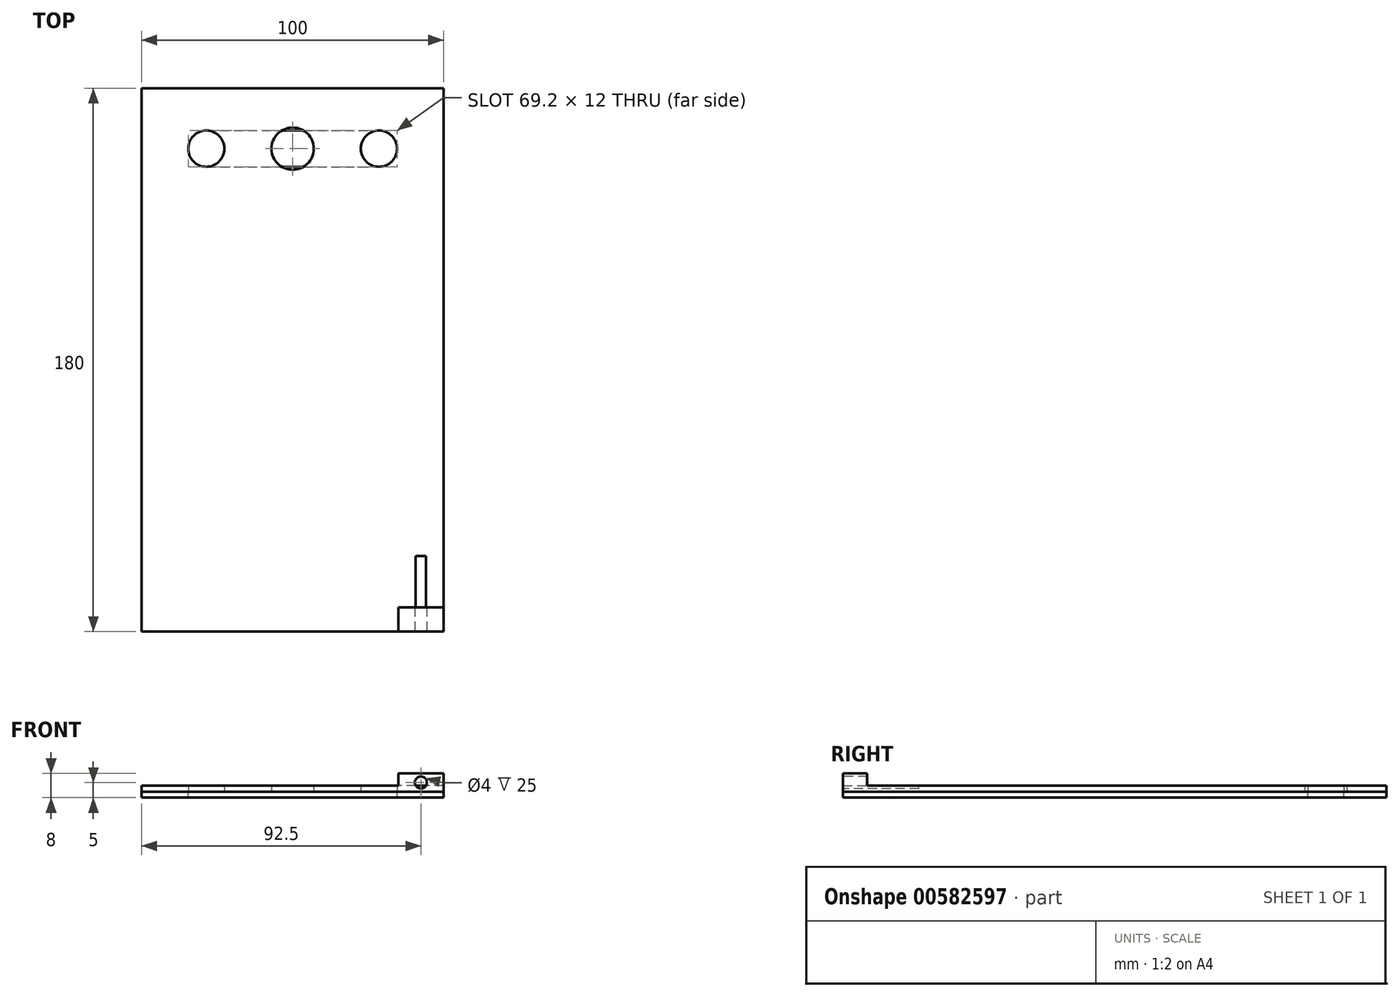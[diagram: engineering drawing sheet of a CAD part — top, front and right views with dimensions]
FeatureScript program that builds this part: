
annotation { "Feature Type Name" : "Feature", "Feature Type Description" : "" }
export const myFeature = defineFeature(function(context is Context, id is Id, definition is map)
    precondition{}
    {
        {
            var Q0;
            Q0=qCreatedBy(makeId("Top.planeOp"),FACE);
            var sketch = newSketch(context, id + "F0", { "sketchPlane" : qUnion([Q0])});
            skLineSegment(sketch, "E0.bottom", {"start": v(-50, -90) * mm, "end": v(50, -90) * mm});
            skLineSegment(sketch, "E0.top", {"start": v(-50, 90) * mm, "end": v(50, 90) * mm});
            skLineSegment(sketch, "E0.left", {"start": v(-50, -90) * mm, "end": v(-50, 90) * mm});
            skLineSegment(sketch, "E0.right", {"start": v(50, -90) * mm, "end": v(50, 90) * mm});
            skPoint(sketch, "E0.middle", {"position": v(0, 0) * mm});
            skCircle(sketch, "E1", {"center": v(0, 70) * mm, "radius": 7 * mm});
            skCircle(sketch, "E2", {"center": v(-28.6, 70) * mm, "radius": 6 * mm});
            skCircle(sketch, "E3.MirrorC", {"center": v(28.6, 70) * mm, "radius": 6 * mm});
            skSolve(sketch);
        }
        {
            var Q0;
            Q0 = qSketchRegion(id + "F0", true);
            extrude(context, id + "F1", {"entities" : qUnion([Q0]), "depth" : 2 * mm, "offsetDistance" : 25 * mm});
        }
        {
            var Q0;
            Q0=makeQuery(id+"F1.opExtrude","CAP_FACE",FACE,{"disambiguationData":[OSD([sQuery(id+"F0.wireOp",EDGE,"E0.bottom"),sQuery(id+"F0.wireOp",EDGE,"E0.top"),sQuery(id+"F0.wireOp",EDGE,"E0.left"),sQuery(id+"F0.wireOp",EDGE,"E0.right"),sQuery(id+"F0.wireOp",EDGE,"E1")])],"isStart":true});
            var sketch = newSketch(context, id + "F2", { "sketchPlane" : qUnion([Q0])});
            skLineSegment(sketch, "E4.bottom", {"start": v(-50, 90) * mm, "end": v(50, 90) * mm});
            skLineSegment(sketch, "E4.top", {"start": v(-50, -90) * mm, "end": v(50, -90) * mm});
            skLineSegment(sketch, "E4.left", {"start": v(-50, 90) * mm, "end": v(-50, -90) * mm});
            skLineSegment(sketch, "E4.right", {"start": v(50, 90) * mm, "end": v(50, -90) * mm});
            skCircle(sketch, "E5.0", {"center": v(-28.6, -70) * mm, "radius": 6 * mm});
            skCircle(sketch, "E6.0", {"center": v(28.6, -70) * mm, "radius": 6 * mm});
            skLineSegment(sketch, "E7", {"start": v(-28.6, -64) * mm, "end": v(28.6, -64) * mm});
            skLineSegment(sketch, "E8", {"start": v(-28.6, -76) * mm, "end": v(28.6, -76) * mm});
            skSolve(sketch);
        }
        {
            var Q0;
            Q0 = qSketchRegion(id + "F2", true);
            extrude(context, id + "F3", {"entities" : qUnion([Q0]), "depth" : 2 * mm, "offsetDistance" : 25 * mm});
        }
        {
            var Q0;
            Q0=makeQuery(id+"F1.opExtrude","CAP_FACE",FACE,{"disambiguationData":[OSD([sQuery(id+"F0.wireOp",EDGE,"E0.bottom"),sQuery(id+"F0.wireOp",EDGE,"E0.top"),sQuery(id+"F0.wireOp",EDGE,"E0.left"),sQuery(id+"F0.wireOp",EDGE,"E0.right"),sQuery(id+"F0.wireOp",EDGE,"E1"),sQuery(id+"F0.wireOp",EDGE,"E2"),sQuery(id+"F0.wireOp",EDGE,"E3.MirrorC")])],"isStart":false});
            var sketch = newSketch(context, id + "F4", { "sketchPlane" : qUnion([Q0])});
            skLineSegment(sketch, "E9.bottom", {"start": v(50, -90) * mm, "end": v(35, -90) * mm});
            skLineSegment(sketch, "E9.top", {"start": v(50, -82) * mm, "end": v(35, -82) * mm});
            skLineSegment(sketch, "E9.left", {"start": v(50, -90) * mm, "end": v(50, -82) * mm});
            skLineSegment(sketch, "E9.right", {"start": v(35, -90) * mm, "end": v(35, -82) * mm});
            skSolve(sketch);
        }
        {
            var Q0;
            Q0 = qSketchRegion(id + "F4", true);
            extrude(context, id + "F5", {"entities" : qUnion([Q0]), "operationType" : NewBodyOperationType.ADD, "depth" : 4 * mm, "offsetDistance" : 25 * mm});
        }
        {
            var Q0;
            Q0=makeQuery(id+"F5.boolean.opBoolean","MERGE",FACE,{"derivedFrom":[makeQuery(id+"F1.opExtrude","SWEPT_FACE",FACE,{"disambiguationData":[OSD([sQuery(id+"F0.wireOp",EDGE,"E0.bottom")])]}),makeQuery(id+"F5.opExtrude","SWEPT_FACE",FACE,{"disambiguationData":[OSD([sQuery(id+"F4.wireOp",EDGE,"E9.bottom")])]})]});
            var sketch = newSketch(context, id + "F6", { "sketchPlane" : qUnion([Q0])});
            skCircle(sketch, "E10", {"center": v(42.5, 3) * mm, "radius": 2 * mm});
            skPoint(sketch, "E11", {"position": v(42.5, 6) * mm});
            skPoint(sketch, "E12", {"position": v(50, 3) * mm});
            skSolve(sketch);
        }
        {
            var Q0;
            Q0 = qSketchRegion(id + "F6", true);
            extrude(context, id + "F7", {"entities" : qUnion([Q0]), "operationType" : NewBodyOperationType.REMOVE, "oppositeDirection" : true, "depth" : 25 * mm, "offsetDistance" : 25 * mm});
        }
    });
